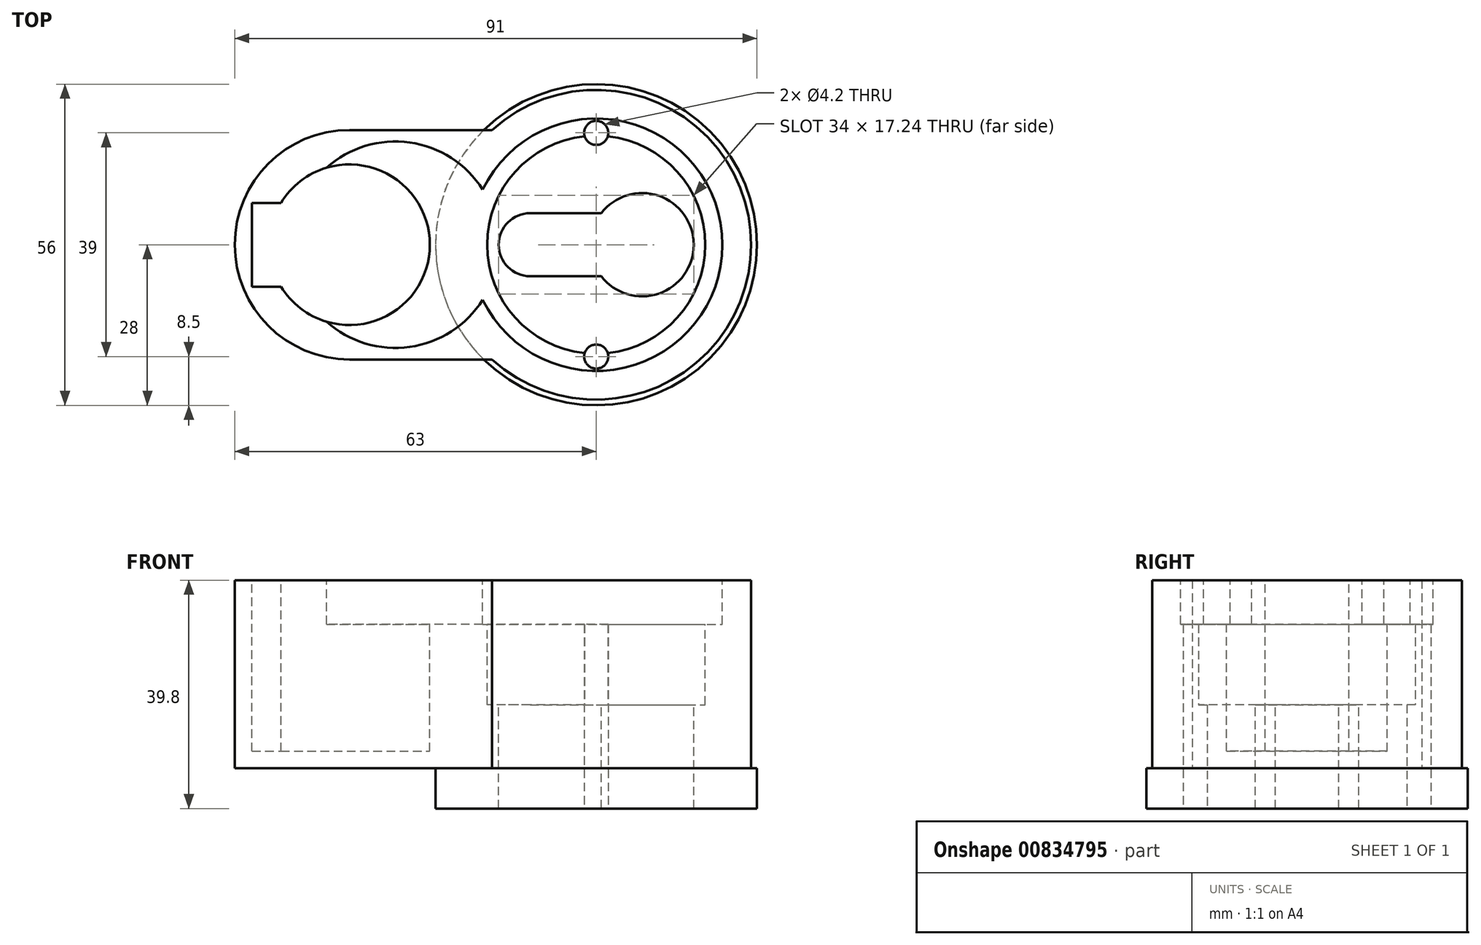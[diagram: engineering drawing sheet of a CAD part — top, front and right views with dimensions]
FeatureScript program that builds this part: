
annotation { "Feature Type Name" : "Feature", "Feature Type Description" : "" }
export const myFeature = defineFeature(function(context is Context, id is Id, definition is map)
    precondition{}
    {
        {
            var Q0;
            Q0=qCreatedBy(makeId("Top.planeOp"),FACE);
            var sketch = newSketch(context, id + "F0", { "sketchPlane" : qUnion([Q0])});
            skArc(sketch, "E0", {"start": v(-18.14, -20) * mm, "mid": v(27, 0) * mm, "end": v(-18.14, 20) * mm});
            skArc(sketch, "E1", {"start": v(-43, 20) * mm, "mid": v(-63, 0) * mm, "end": v(-43, -20) * mm});
            skLineSegment(sketch, "E2", {"start": v(-43, 20) * mm, "end": v(-18.14, 20) * mm});
            skLineSegment(sketch, "E3", {"start": v(-43, -20) * mm, "end": v(-18.14, -20) * mm});
            skSolve(sketch);
        }
        {
            var Q0;
            Q0 = qSketchRegion(id + "F0", true);
            extrude(context, id + "F1", {"entities" : qUnion([Q0]), "depth" : 32.8 * mm, "offsetDistance" : 25 * mm});
        }
        {
            var Q0;
            Q0=makeQuery(id+"F1.opExtrude","CAP_FACE",FACE,{"disambiguationData":[OSD([sQuery(id+"F0.wireOp",EDGE,"E0"),sQuery(id+"F0.wireOp",EDGE,"E1"),sQuery(id+"F0.wireOp",EDGE,"E2"),sQuery(id+"F0.wireOp",EDGE,"E3")])],"isStart":false});
            var sketch = newSketch(context, id + "F2", { "sketchPlane" : qUnion([Q0])});
            skCircle(sketch, "E4", {"center": v(0, 0) * mm, "radius": 22 * mm});
            skSolve(sketch);
        }
        {
            var Q0;
            Q0 = qSketchRegion(id + "F2", true);
            extrude(context, id + "F3", {"entities" : qUnion([Q0]), "operationType" : NewBodyOperationType.REMOVE, "oppositeDirection" : true, "depth" : 7.7 * mm, "offsetDistance" : 25 * mm});
        }
        {
            var Q0;
            Q0=makeQuery(id+"F3.boolean.opBoolean","COPY",FACE,{"derivedFrom":makeQuery(id+"F3.opExtrude","CAP_FACE",FACE,{"disambiguationData":[OSD([sQuery(id+"F2.wireOp",EDGE,"E4")])],"isStart":false})});
            var sketch = newSketch(context, id + "F4", { "sketchPlane" : qUnion([Q0])});
            skCircle(sketch, "E5", {"center": v(0, 0) * mm, "radius": 19 * mm});
            skSolve(sketch);
        }
        {
            var Q0;
            Q0 = qSketchRegion(id + "F4", true);
            extrude(context, id + "F5", {"entities" : qUnion([Q0]), "operationType" : NewBodyOperationType.REMOVE, "oppositeDirection" : true, "depth" : 14 * mm, "offsetDistance" : 25 * mm});
        }
        {
            var Q0;
            Q0=makeQuery(id+"F1.opExtrude","CAP_FACE",FACE,{"disambiguationData":[OSD([sQuery(id+"F0.wireOp",EDGE,"E0"),sQuery(id+"F0.wireOp",EDGE,"E1"),sQuery(id+"F0.wireOp",EDGE,"E2"),sQuery(id+"F0.wireOp",EDGE,"E3")])],"isStart":false});
            var sketch = newSketch(context, id + "F6", { "sketchPlane" : qUnion([Q0])});
            skArc(sketch, "E6", {"start": v(-54.95, -7.3) * mm, "mid": v(-29, 0) * mm, "end": v(-54.95, 7.3) * mm});
            skLineSegment(sketch, "E7", {"start": v(-60, 7.3) * mm, "end": v(-60, -7.3) * mm});
            skLineSegment(sketch, "E8", {"start": v(-60, -7.3) * mm, "end": v(-54.95, -7.3) * mm});
            skLineSegment(sketch, "E9", {"start": v(-60, 7.3) * mm, "end": v(-54.95, 7.3) * mm});
            skLineSegment(sketch, "E10", {"start": v(-60, 0) * mm, "end": v(-66.16, 0) * mm, "construction": true});
            skSolve(sketch);
        }
        {
            var Q0;
            Q0 = qSketchRegion(id + "F6", true);
            extrude(context, id + "F7", {"entities" : qUnion([Q0]), "operationType" : NewBodyOperationType.REMOVE, "oppositeDirection" : true, "depth" : 29.8 * mm, "offsetDistance" : 25 * mm});
        }
        {
            var Q0;
            Q0=makeQuery(id+"F1.opExtrude","CAP_FACE",FACE,{"disambiguationData":[OSD([sQuery(id+"F0.wireOp",EDGE,"E0"),sQuery(id+"F0.wireOp",EDGE,"E1"),sQuery(id+"F0.wireOp",EDGE,"E2"),sQuery(id+"F0.wireOp",EDGE,"E3")])],"isStart":false});
            var sketch = newSketch(context, id + "F8", { "sketchPlane" : qUnion([Q0])});
            skCircle(sketch, "E11", {"center": v(-35, 0) * mm, "radius": 18 * mm});
            skSolve(sketch);
        }
        {
            var Q0;
            Q0 = qSketchRegion(id + "F8", true);
            extrude(context, id + "F9", {"entities" : qUnion([Q0]), "operationType" : NewBodyOperationType.REMOVE, "oppositeDirection" : true, "depth" : 7.7 * mm, "offsetDistance" : 25 * mm});
        }
        {
            var Q0;
            Q0=makeQuery(id+"F1.opExtrude","CAP_FACE",FACE,{"disambiguationData":[OSD([sQuery(id+"F0.wireOp",EDGE,"E0"),sQuery(id+"F0.wireOp",EDGE,"E1"),sQuery(id+"F0.wireOp",EDGE,"E2"),sQuery(id+"F0.wireOp",EDGE,"E3")])],"isStart":true});
            var sketch = newSketch(context, id + "F10", { "sketchPlane" : qUnion([Q0])});
            skCircle(sketch, "E12", {"center": v(0, 0) * mm, "radius": 28 * mm});
            skLineSegment(sketch, "E13", {"start": v(0, 0) * mm, "end": v(8, 0) * mm, "construction": true});
            skArc(sketch, "E14", {"start": v(0.88, -5.5) * mm, "mid": v(17, 0) * mm, "end": v(0.88, 5.5) * mm});
            skArc(sketch, "E15", {"start": v(-11.5, 5.5) * mm, "mid": v(-17, 0) * mm, "end": v(-11.5, -5.5) * mm});
            skLineSegment(sketch, "E16", {"start": v(-11.5, 5.5) * mm, "end": v(0.88, 5.5) * mm});
            skLineSegment(sketch, "E17", {"start": v(-11.5, -5.5) * mm, "end": v(0.88, -5.5) * mm});
            skSolve(sketch);
        }
        {
            var Q0;
            Q0 = qSketchRegion(id + "F10", true);
            extrude(context, id + "F11", {"entities" : qUnion([Q0]), "operationType" : NewBodyOperationType.ADD, "depth" : 7 * mm, "offsetDistance" : 25 * mm});
        }
        {
            var Q0;
            Q0=makeQuery(id+"F11.opExtrude","CAP_FACE",FACE,{"disambiguationData":[OSD([sQuery(id+"F10.wireOp",EDGE,"E12"),sQuery(id+"F10.wireOp",EDGE,"E14"),sQuery(id+"F10.wireOp",EDGE,"E15"),sQuery(id+"F10.wireOp",EDGE,"E16"),sQuery(id+"F10.wireOp",EDGE,"E17")])],"isStart":false});
            var sketch = newSketch(context, id + "F12", { "sketchPlane" : qUnion([Q0])});
            skLineSegment(sketch, "E18", {"start": v(0, 0) * mm, "end": v(0, -19.5) * mm, "construction": true});
            skLineSegment(sketch, "E19", {"start": v(0, 0) * mm, "end": v(5.6, 0) * mm, "construction": true});
            skCircle(sketch, "E20", {"center": v(0, -19.5) * mm, "radius": 2.1 * mm});
            skLineSegment(sketch, "E21.MirrorCS", {"start": v(0, 0) * mm, "end": v(0, 19.5) * mm, "construction": true});
            skCircle(sketch, "E22.MirrorC", {"center": v(0, 19.5) * mm, "radius": 2.1 * mm});
            skSolve(sketch);
        }
        {
            var Q0;
            Q0 = qSketchRegion(id + "F12", true);
            extrude(context, id + "F13", {"entities" : qUnion([Q0]), "operationType" : NewBodyOperationType.REMOVE, "endBound" : BoundingType.THROUGH_ALL, "oppositeDirection" : true, "depth" : 25 * mm, "offsetDistance" : 25 * mm});
        }
        {
            var Q0;
            Q0=makeQuery(id+"F11.boolean.opBoolean","SPLIT",FACE,{"disambiguationData":[TD([makeQuery(id+"F11.opExtrude","SWEPT_FACE",FACE,{"disambiguationData":[OSD([sQuery(id+"F10.wireOp",EDGE,"E14")])]})])],"derivedFrom":makeQuery(id+"F1.opExtrude","CAP_FACE",FACE,{"disambiguationData":[OSD([sQuery(id+"F0.wireOp",EDGE,"E0"),sQuery(id+"F0.wireOp",EDGE,"E1"),sQuery(id+"F0.wireOp",EDGE,"E2"),sQuery(id+"F0.wireOp",EDGE,"E3")])],"isStart":true})});
            extrude(context, id + "F14", {"entities" : qUnion([Q0]), "operationType" : NewBodyOperationType.REMOVE, "endBound" : BoundingType.UP_TO_NEXT, "oppositeDirection" : true, "depth" : 25 * mm, "offsetDistance" : 25 * mm});
        }
    });
